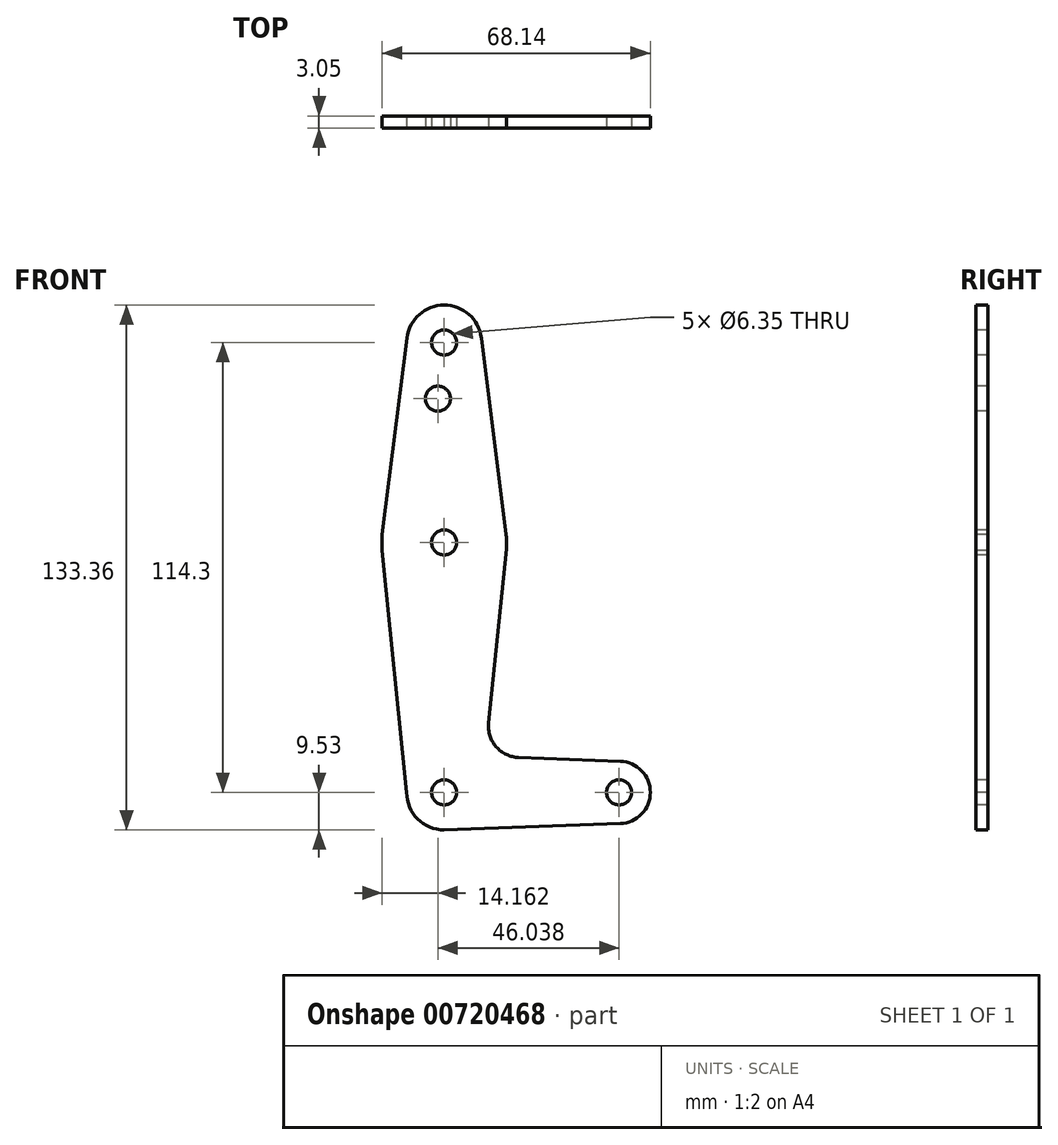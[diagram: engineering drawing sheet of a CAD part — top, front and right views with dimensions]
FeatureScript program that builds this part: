
annotation { "Feature Type Name" : "Feature", "Feature Type Description" : "" }
export const myFeature = defineFeature(function(context is Context, id is Id, definition is map)
    precondition{}
    {
        {
            var Q0;
            Q0=qCreatedBy(makeId("Front.planeOp"),FACE);
            var sketch = newSketch(context, id + "F0", { "sketchPlane" : qUnion([Q0])});
            skLineSegment(sketch, "E0", {"start": v(0, 0) * mm, "end": v(0, 114.3) * mm, "construction": true});
            skLineSegment(sketch, "E1", {"start": v(0, 0) * mm, "end": v(44.45, 0) * mm, "construction": true});
            skCircle(sketch, "E2", {"center": v(0, 114.3) * mm, "radius": 9.53 * mm});
            skCircle(sketch, "E3", {"center": v(0, 0) * mm, "radius": 9.53 * mm});
            skCircle(sketch, "E4", {"center": v(44.45, 0) * mm, "radius": 7.94 * mm});
            skCircle(sketch, "E5", {"center": v(0, 63.5) * mm, "radius": 15.88 * mm});
            skLineSegment(sketch, "E6", {"start": v(-15.75, 65.48) * mm, "end": v(-15.75, 61.47) * mm});
            skLineSegment(sketch, "E7", {"start": v(0, -9.53) * mm, "end": v(44.73, -7.93) * mm});
            skLineSegment(sketch, "E8", {"start": v(15.75, 65.48) * mm, "end": v(15.98, 63.7) * mm});
            skLineSegment(sketch, "E9", {"start": v(-9.52, 0) * mm, "end": v(-15.75, 61.47) * mm});
            skLineSegment(sketch, "E10", {"start": v(11.3, 17.6) * mm, "end": v(15.98, 63.7) * mm});
            skLineSegment(sketch, "E11", {"start": v(18.93, 8.85) * mm, "end": v(44.73, 7.93) * mm});
            skLineSegment(sketch, "E12", {"start": v(-9.45, 115.5) * mm, "end": v(-15.75, 65.48) * mm});
            skLineSegment(sketch, "E13", {"start": v(9.45, 115.5) * mm, "end": v(15.75, 65.48) * mm});
            skCircle(sketch, "E14", {"center": v(0, 114.3) * mm, "radius": 3.18 * mm});
            skCircle(sketch, "E15", {"center": v(-1.59, 100.03) * mm, "radius": 3.18 * mm});
            skCircle(sketch, "E16", {"center": v(0, 63.5) * mm, "radius": 3.18 * mm});
            skCircle(sketch, "E17", {"center": v(0, 0) * mm, "radius": 3.18 * mm});
            skCircle(sketch, "E18", {"center": v(44.45, 0) * mm, "radius": 3.18 * mm});
            skPoint(sketch, "E19.newPointB", {"position": v(0, 9.53) * mm});
            skArc(sketch, "E19.filletArc", {"start": v(11.3, 17.6) * mm, "mid": v(13.22, 11.57) * mm, "end": v(18.93, 8.85) * mm});
            skSolve(sketch);
        }
        {
            var Q0;
            {var subQ0=sQuery(id+"F0.wireOp",EDGE,"E9");Q0=makeQuery(id+"F0.imprint","IMPRINT",FACE,{"disambiguationData":[TD([[makeQuery(id+"F0.imprint","IMPRINT",EDGE,{"derivedFrom":subQ0}),-1.0]])]});}
            var Q1;
            Q1=makeQuery(id+"F0.imprint","IMPRINT",FACE,{"disambiguationData":[TD([[makeQuery(id+"F0.imprint","IMPRINT",EDGE,{"derivedFrom":sQuery(id+"F0.wireOp",EDGE,"E17")}),-1.0]])]});
            var Q2;
            Q2=makeQuery(id+"F0.imprint","IMPRINT",FACE,{"disambiguationData":[TD([[makeQuery(id+"F0.imprint","IMPRINT",EDGE,{"derivedFrom":sQuery(id+"F0.wireOp",EDGE,"E18")}),-1.0]])]});
            var Q3;
            Q3=makeQuery(id+"F0.imprint","IMPRINT",FACE,{"disambiguationData":[TD([[makeQuery(id+"F0.imprint","IMPRINT",EDGE,{"derivedFrom":sQuery(id+"F0.wireOp",EDGE,"E16")}),-1.0]])]});
            var Q4;
            Q4=makeQuery(id+"F0.imprint","IMPRINT",FACE,{"disambiguationData":[TD([[makeQuery(id+"F0.imprint","IMPRINT",EDGE,{"derivedFrom":sQuery(id+"F0.wireOp",EDGE,"E14")}),-1.0]])]});
            var Q5;
            {var subQ0=sQuery(id+"F0.wireOp",EDGE,"E12");Q5=makeQuery(id+"F0.imprint","IMPRINT",FACE,{"disambiguationData":[TD([[makeQuery(id+"F0.imprint","IMPRINT",EDGE,{"derivedFrom":subQ0}),1.0]])]});}
            extrude(context, id + "F1", {"entities" : qUnion([Q0, Q1, Q2, Q3, Q4, Q5]), "surfaceOperationType" : NewSurfaceOperationType.ADD, "oppositeDirection" : true, "depth" : 3.05 * mm, "offsetDistance" : 25.4 * mm});
        }
    });
